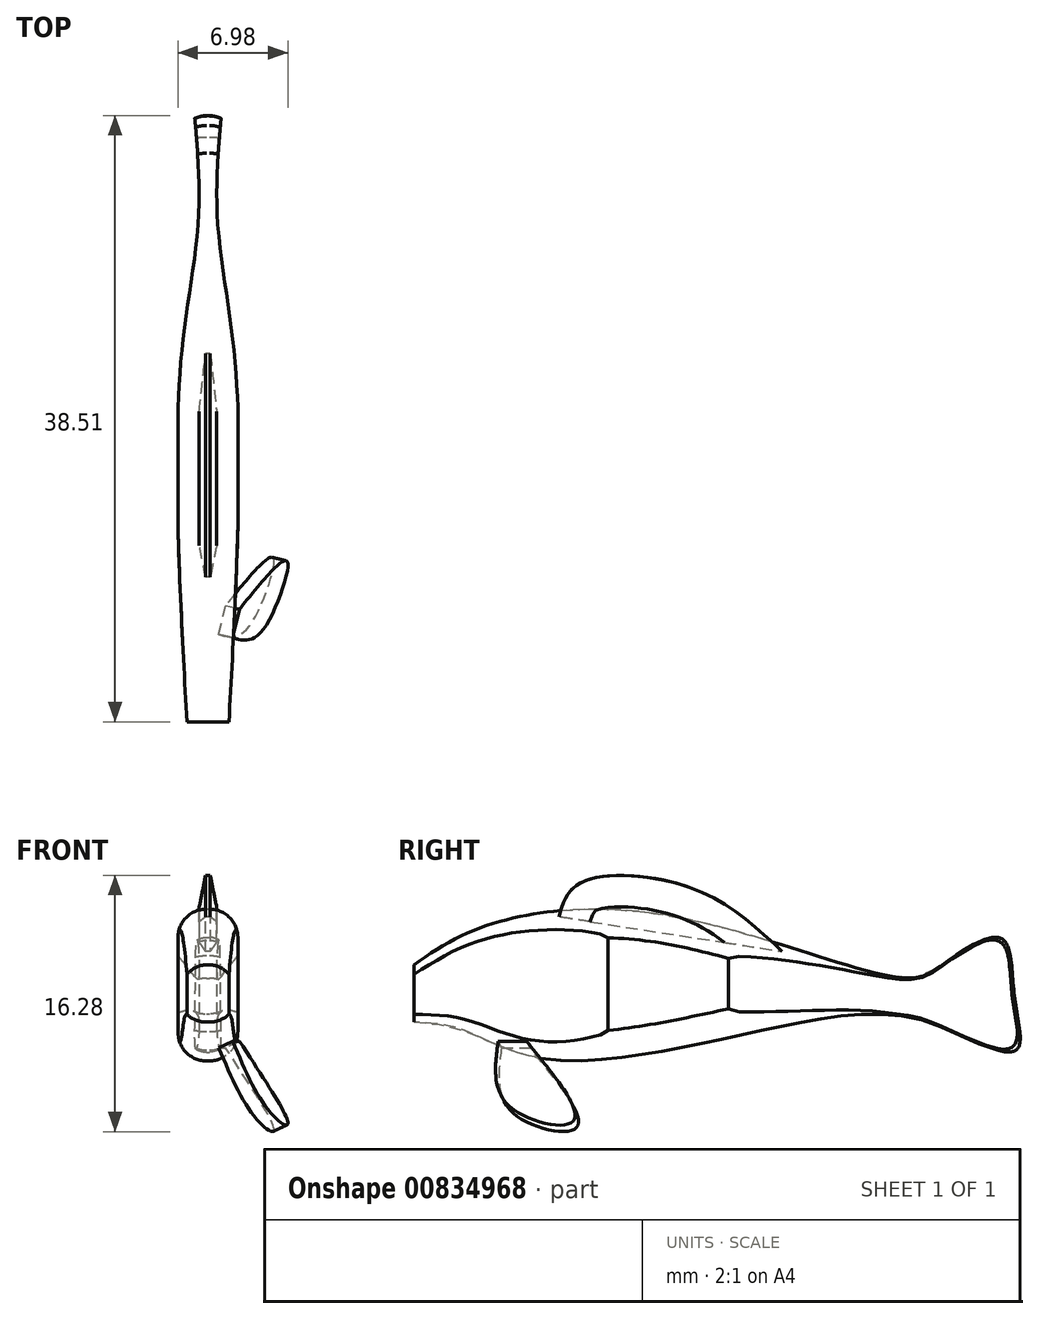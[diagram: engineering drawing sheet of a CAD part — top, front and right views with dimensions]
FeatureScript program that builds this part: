
annotation { "Feature Type Name" : "Feature", "Feature Type Description" : "" }
export const myFeature = defineFeature(function(context is Context, id is Id, definition is map)
    precondition{}
    {
        {
            var Q0;
            Q0=qCreatedBy(makeId("Right.planeOp"),FACE);
            var sketch = newSketch(context, id + "F0", { "sketchPlane" : qUnion([Q0])});
            skFitSpline(sketch, "E0", {"points": [v(0, 2.1) * mm, v(4.2, 4.44) * mm, v(16.15, 5.23) * mm, v(31.19, 1.25) * mm, v(33.78, 2.25) * mm, v(37.26, 3.8) * mm, v(38.16, 0) * mm, v(38.16, -3.38) * mm, v(33.23, -1.74) * mm, v(31.24, -1.19) * mm, v(26.75, -1.19) * mm, v(9.23, -3.98) * mm, v(3.1, -2.04) * mm, v(0, -1.54) * mm], "startDerivative": vector(52.69, 36.77) * mm, "endDerivative": vector(-53.72, 3.44) * mm});
            skLineSegment(sketch, "E1", {"start": v(0, 2.1) * mm, "end": v(0, -1.54) * mm});
            skLineSegment(sketch, "E2.bottom", {"start": v(0, -6.27) * mm, "end": v(40, -6.27) * mm, "construction": true});
            skLineSegment(sketch, "E2.top", {"start": v(0, 9.22) * mm, "end": v(40, 9.22) * mm, "construction": true});
            skLineSegment(sketch, "E2.left", {"start": v(0, -6.27) * mm, "end": v(0, 9.22) * mm, "construction": true});
            skLineSegment(sketch, "E2.right", {"start": v(40, -6.27) * mm, "end": v(40, 9.22) * mm, "construction": true});
            skSolve(sketch);
        }
        {
            var Q0;
            Q0 = qSketchRegion(id + "F0", true);
            extrude(context, id + "F1", {"entities" : qUnion([Q0]), "endBound" : BoundingType.SYMMETRIC, "depth" : 3.8 * mm, "offsetDistance" : 25 * mm});
        }
        {
            var Q0;
            Q0=makeQuery(id+"F1.opExtrude","CAP_EDGE",EDGE,{"disambiguationData":[OSD([sQuery(id+"F0.wireOp",EDGE,"E0")])],"isStart":false});
            var Q1;
            Q1=makeQuery(id+"F1.opExtrude","CAP_EDGE",EDGE,{"disambiguationData":[OSD([sQuery(id+"F0.wireOp",EDGE,"E0")])],"isStart":true});
            fillet(context, id + "F2", {"entities" : qUnion([Q0, Q1]), "radius" : 1.8 * mm, "tangentPropagation" : true, "allowEdgeOverflow" : false});
        }
        {
            var Q0;
            Q0=qCreatedBy(makeId("Top.planeOp"),FACE);
            var sketch = newSketch(context, id + "F3", { "sketchPlane" : qUnion([Q0])});
            skFitSpline(sketch, "E3", {"points": [v(-1, 39.94) * mm, v(-0.6, 31.95) * mm, v(-1.77, 22.27) * mm, v(-1.34, 0) * mm], "startDerivative": vector(3.1, -30.27) * mm, "endDerivative": vector(3, -55.58) * mm});
            skLineSegment(sketch, "E4", {"start": v(-1, 39.94) * mm, "end": v(-5.04, 39.94) * mm});
            skLineSegment(sketch, "E5", {"start": v(-5.04, 39.94) * mm, "end": v(-5.04, 0) * mm});
            skLineSegment(sketch, "E6", {"start": v(-5.04, 0) * mm, "end": v(-1.34, 0) * mm});
            skLineSegment(sketch, "E7.MirrorCS", {"start": v(5.04, 39.94) * mm, "end": v(5.04, 0) * mm});
            skLineSegment(sketch, "E8.MirrorCS", {"start": v(1, 39.94) * mm, "end": v(5.04, 39.94) * mm});
            skLineSegment(sketch, "E9.MirrorCS", {"start": v(5.04, 0) * mm, "end": v(1.34, 0) * mm});
            skFitSpline(sketch, "E10.MirrorCS", {"points": [v(1, 39.94) * mm, v(0.6, 31.95) * mm, v(1.77, 22.27) * mm, v(1.34, 0) * mm], "startDerivative": vector(-3.1, -30.27) * mm, "endDerivative": vector(-3, -55.58) * mm});
            skSolve(sketch);
        }
        {
            var Q0;
            Q0 = qSketchRegion(id + "F3", true);
            extrude(context, id + "F4", {"entities" : qUnion([Q0]), "operationType" : NewBodyOperationType.REMOVE, "endBound" : BoundingType.THROUGH_ALL, "oppositeDirection" : true, "depth" : 25 * mm, "offsetDistance" : 25 * mm, "hasSecondDirection" : true, "secondDirectionBound" : SecondDirectionBoundingType.THROUGH_ALL, "secondDirectionOppositeDirection" : false, "secondDirectionDepth" : 25 * mm});
        }
        {
            var Q0;
            Q0=qCreatedBy(makeId("Right.planeOp"),FACE);
            var sketch = newSketch(context, id + "F5", { "sketchPlane" : qUnion([Q0])});
            skFitSpline(sketch, "E11", {"points": [v(9.2, 5.14) * mm, v(10.56, 7.3) * mm, v(17.65, 6.96) * mm, v(23.39, 2.95) * mm], "startDerivative": vector(3.15, 10.87) * mm, "endDerivative": vector(13, -12.2) * mm});
            skLineSegment(sketch, "E12", {"start": v(9.2, 5.14) * mm, "end": v(23.39, 2.95) * mm});
            skSolve(sketch);
        }
        {
            var Q0;
            Q0 = qSketchRegion(id + "F5", true);
            extrude(context, id + "F6", {"entities" : qUnion([Q0]), "endBound" : BoundingType.SYMMETRIC, "depth" : 1.1 * mm, "offsetDistance" : 25 * mm});
        }
        {
            var Q0;
            Q0=makeQuery(id+"F6.opExtrude","CAP_EDGE",EDGE,{"disambiguationData":[OSD([sQuery(id+"F5.wireOp",EDGE,"E11")])],"isStart":false});
            var Q1;
            Q1=makeQuery(id+"F6.opExtrude","CAP_EDGE",EDGE,{"disambiguationData":[OSD([sQuery(id+"F5.wireOp",EDGE,"E11")])],"isStart":true});
            chamfer(context, id + "F7", {"entities" : qUnion([Q0, Q1]), "chamferType" : ChamferType.TWO_OFFSETS, "width1" : .4 * mm, "oppositeDirection" : false, "width2" : 2 * mm, "tangentPropagation" : true});
        }
        {
            var Q0;
            Q0=qCreatedBy(makeId("Right.planeOp"),FACE);
            var sketch = newSketch(context, id + "F8", { "sketchPlane" : qUnion([Q0])});
            skFitSpline(sketch, "E13", {"points": [v(5.85, -6.62) * mm, v(9.38, -9.63) * mm, v(13.5, -8.11) * mm, v(7.36, -5.55) * mm], "startDerivative": vector(8.8, -13.34) * mm, "endDerivative": vector(-25.08, 6.3) * mm});
            skLineSegment(sketch, "E14", {"start": v(5.85, -6.62) * mm, "end": v(7.36, -5.55) * mm});
            skSolve(sketch);
        }
        {
            var Q0;
            Q0 = qSketchRegion(id + "F8", true);
            extrude(context, id + "F9", {"entities" : qUnion([Q0]), "endBound" : BoundingType.SYMMETRIC, "depth" : 1 * mm, "offsetDistance" : 25 * mm});
        }
        {
            var Q0;
            Q0=makeQuery(id+"F9.opExtrude","SWEPT_BODY",BODY,{"disambiguationData":[OSD([sQuery(id+"F8.wireOp",EDGE,"E13"),sQuery(id+"F8.wireOp",EDGE,"E14")])]});
            transform(context, id + "F10", {"entities" : qUnion([Q0]), "transformType" : TransformType.TRANSLATION_3D, "dx" : 1.61 * mm, "dy" : 0 * mm, "dz" : 2.38 * mm, "makeCopy" : false});
        }
        {
            var Q0;
            Q0=makeQuery(id+"F9.opExtrude","SWEPT_BODY",BODY,{"disambiguationData":[OSD([sQuery(id+"F8.wireOp",EDGE,"E13"),sQuery(id+"F8.wireOp",EDGE,"E14")])]});
            var Q1;
            {var subQ0=sQuery(id+"F8.wireOp",EDGE,"E14");var subQ1=sQuery(id+"F8.wireOp",EDGE,"E13");Q1=makeQuery(id+"F9.opExtrude","SWEPT_EDGE",EDGE,{"disambiguationData":[OSD([subQ1,subQ0]),TDD([makeQuery(id+"F8.imprint","INTERSECT",VERTEX,{"disambiguationData":[OD(1.0)],"derivedFrom":[subQ1,subQ0]})])]});}
            transform(context, id + "F11", {"entities" : qUnion([Q0]), "transformType" : TransformType.ROTATION, "transformAxis" : qUnion([Q1]), "angle" : 7.9 * degree, "makeCopy" : false});
        }
        {
            var Q0;
            Q0=makeQuery(id+"F9.opExtrude","SWEPT_BODY",BODY,{"disambiguationData":[OSD([sQuery(id+"F8.wireOp",EDGE,"E13"),sQuery(id+"F8.wireOp",EDGE,"E14")])]});
            var Q1;
            Q1=makeQuery(id+"F9.opExtrude","CAP_EDGE",EDGE,{"disambiguationData":[OSD([sQuery(id+"F8.wireOp",EDGE,"E14")])],"isStart":true});
            transform(context, id + "F12", {"entities" : qUnion([Q0]), "transformType" : TransformType.ROTATION, "transformAxis" : qUnion([Q1]), "angle" : 27.59 * degree, "oppositeDirection" : true, "makeCopy" : false});
        }
        {
            var Q0;
            Q0=makeQuery(id+"F9.opExtrude","SWEPT_BODY",BODY,{"disambiguationData":[OSD([sQuery(id+"F8.wireOp",EDGE,"E13"),sQuery(id+"F8.wireOp",EDGE,"E14")])]});
            var Q1;
            {var subQ0=sQuery(id+"F8.wireOp",EDGE,"E14");var subQ1=sQuery(id+"F8.wireOp",EDGE,"E13");Q1=makeQuery(id+"F9.opExtrude","SWEPT_EDGE",EDGE,{"disambiguationData":[OSD([subQ1,subQ0]),TDD([makeQuery(id+"F8.imprint","INTERSECT",VERTEX,{"disambiguationData":[OD(1.0)],"derivedFrom":[subQ1,subQ0]})])]});}
            transform(context, id + "F13", {"entities" : qUnion([Q0]), "transformType" : TransformType.ROTATION, "transformAxis" : qUnion([Q1]), "angle" : 30 * degree, "makeCopy" : false});
        }
    });
